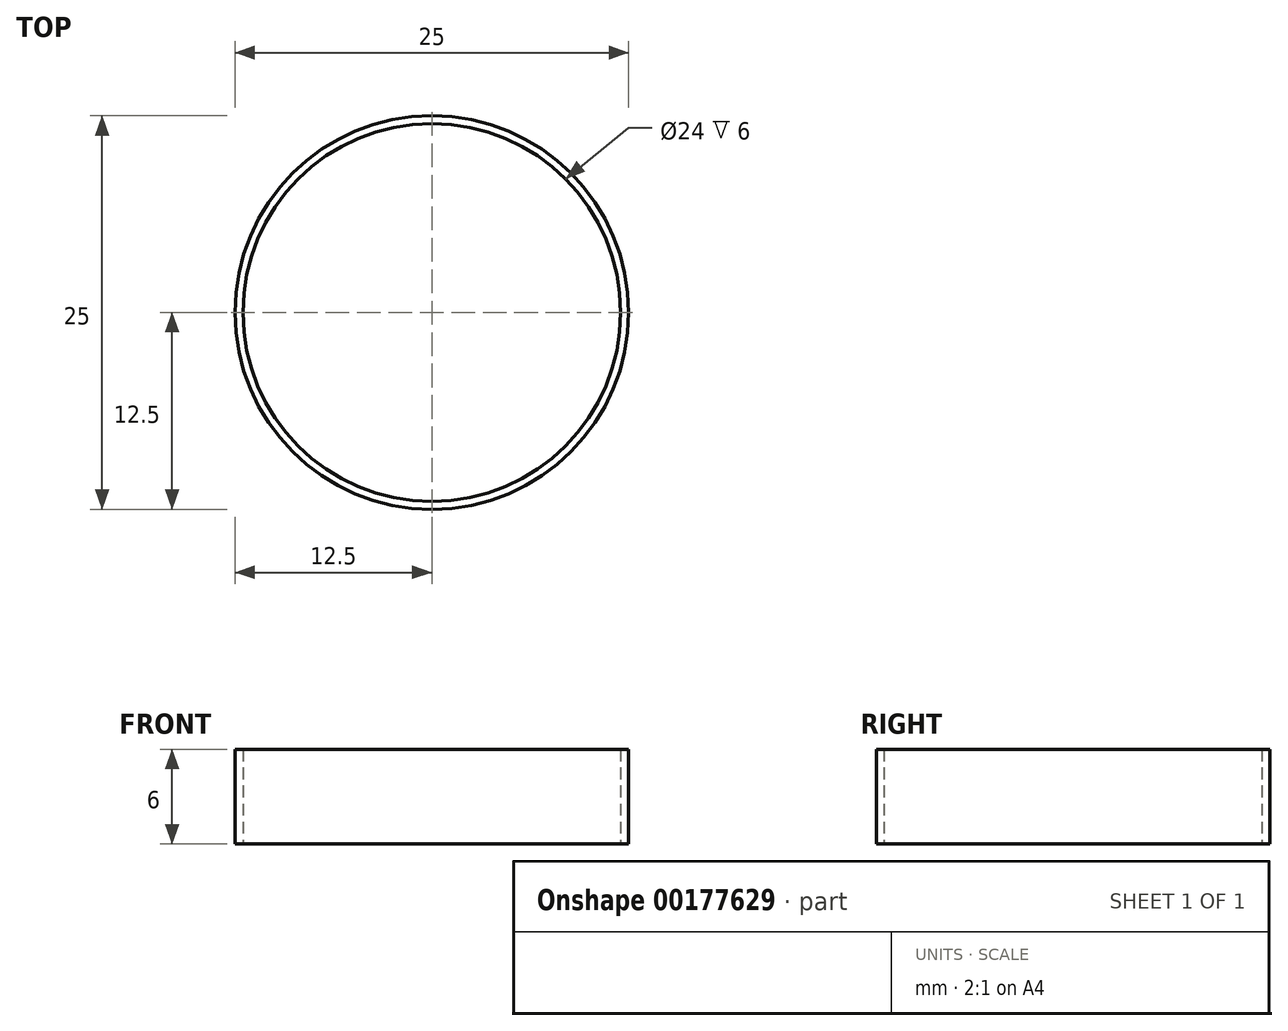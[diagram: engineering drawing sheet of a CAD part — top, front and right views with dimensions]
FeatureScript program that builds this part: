
annotation { "Feature Type Name" : "Feature", "Feature Type Description" : "" }
export const myFeature = defineFeature(function(context is Context, id is Id, definition is map)
    precondition{}
    {
        {
            var Q0;
            Q0=qCreatedBy(makeId("Top.planeOp"),FACE);
            var sketch = newSketch(context, id + "F0", { "sketchPlane" : qUnion([Q0])});
            skCircle(sketch, "E0", {"center": v(0, 0) * mm, "radius": 12 * mm});
            skCircle(sketch, "E1", {"center": v(0, 0) * mm, "radius": 12.5 * mm});
            skSolve(sketch);
        }
        {
            var Q0;
            Q0 = qSketchRegion(id + "F0", true);
            extrude(context, id + "F1", {"entities" : qUnion([Q0]), "depth" : 6 * mm});
        }
    });
